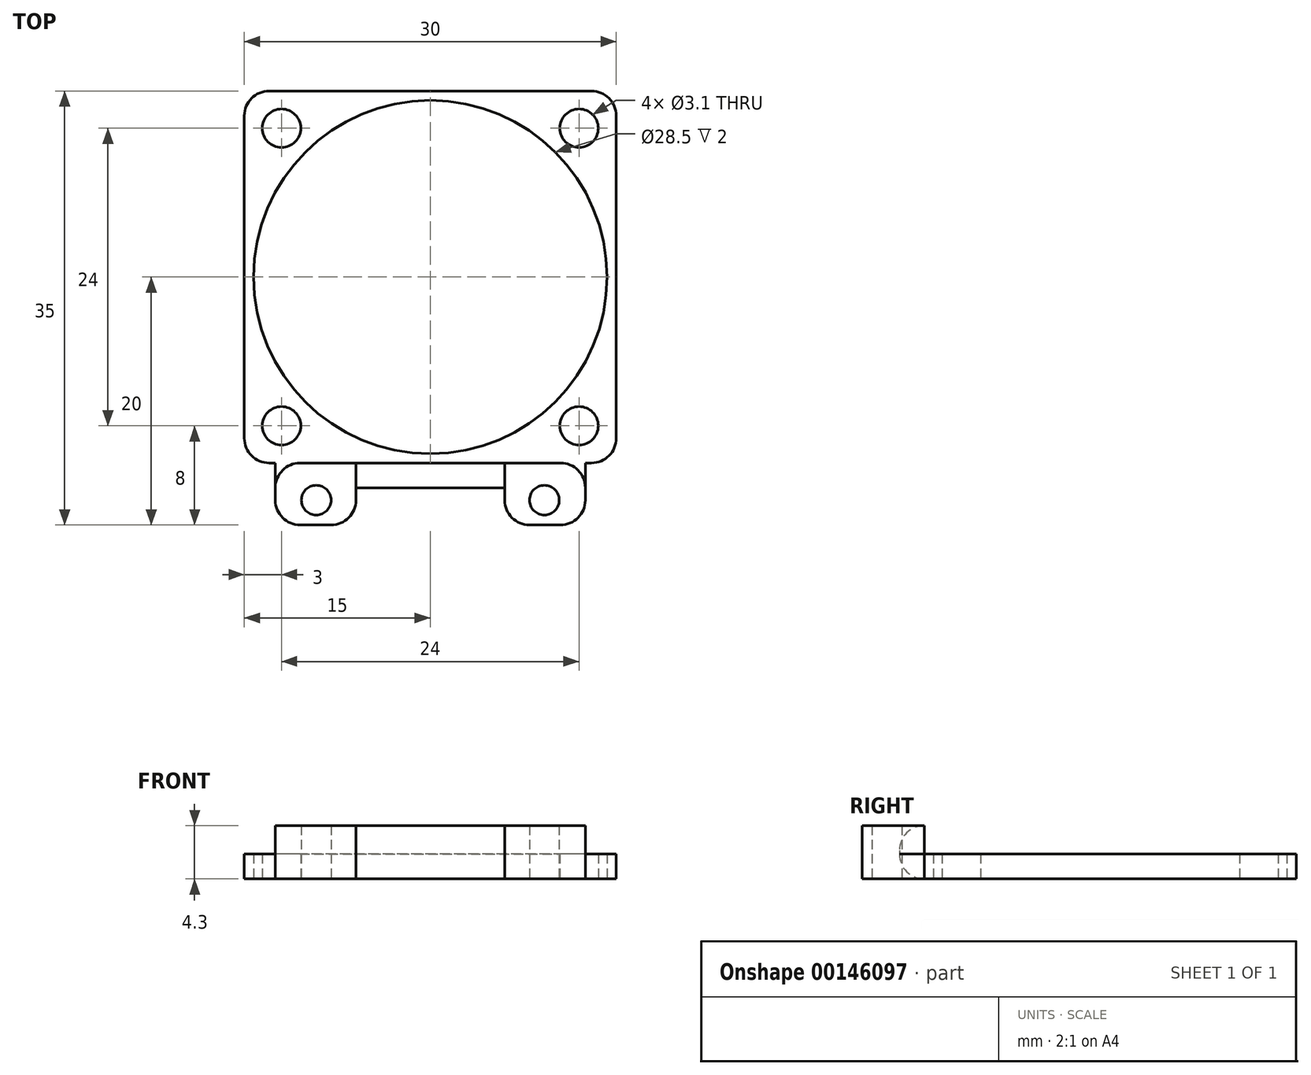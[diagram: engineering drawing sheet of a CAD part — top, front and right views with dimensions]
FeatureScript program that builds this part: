
annotation { "Feature Type Name" : "Feature", "Feature Type Description" : "" }
export const myFeature = defineFeature(function(context is Context, id is Id, definition is map)
    precondition{}
    {
        {
            var Q0;
            Q0=qCreatedBy(makeId("Top.planeOp"),FACE);
            var sketch = newSketch(context, id + "F0", { "sketchPlane" : qUnion([Q0])});
            skLineSegment(sketch, "E0.bottom", {"start": v(15, -15) * mm, "end": v(-15, -15) * mm});
            skLineSegment(sketch, "E0.top", {"start": v(15, 15) * mm, "end": v(-15, 15) * mm});
            skLineSegment(sketch, "E0.left", {"start": v(15, -15) * mm, "end": v(15, 15) * mm});
            skLineSegment(sketch, "E0.right", {"start": v(-15, -15) * mm, "end": v(-15, 15) * mm});
            skPoint(sketch, "E0.middle", {"position": v(0, 0) * mm});
            skLineSegment(sketch, "E1.bottom", {"start": v(12, -12) * mm, "end": v(-12, -12) * mm, "construction": true});
            skLineSegment(sketch, "E1.top", {"start": v(12, 12) * mm, "end": v(-12, 12) * mm, "construction": true});
            skLineSegment(sketch, "E1.left", {"start": v(12, -12) * mm, "end": v(12, 12) * mm, "construction": true});
            skLineSegment(sketch, "E1.right", {"start": v(-12, -12) * mm, "end": v(-12, 12) * mm, "construction": true});
            skCircle(sketch, "E2", {"center": v(-12, 12) * mm, "radius": 1.55 * mm});
            skCircle(sketch, "E3", {"center": v(12, 12) * mm, "radius": 1.55 * mm});
            skCircle(sketch, "E4", {"center": v(12, -12) * mm, "radius": 1.55 * mm});
            skCircle(sketch, "E5", {"center": v(-12, -12) * mm, "radius": 1.55 * mm});
            skLineSegment(sketch, "E6", {"start": v(-14.96, -20) * mm, "end": v(-6, -20) * mm, "construction": true});
            skLineSegment(sketch, "E7.bottom", {"start": v(-15, -15) * mm, "end": v(15, -15) * mm});
            skLineSegment(sketch, "E7.top", {"start": v(-6, -17) * mm, "end": v(6, -17) * mm});
            skLineSegment(sketch, "E8.bottom", {"start": v(-12.5, -15) * mm, "end": v(12.5, -15) * mm});
            skLineSegment(sketch, "E8.top", {"start": v(-12.5, -20) * mm, "end": v(-6, -20) * mm});
            skLineSegment(sketch, "E8.left", {"start": v(-12.5, -15) * mm, "end": v(-12.5, -20) * mm});
            skLineSegment(sketch, "E8.right", {"start": v(12.5, -15) * mm, "end": v(12.5, -20) * mm});
            skLineSegment(sketch, "E9.bottom", {"start": v(-6, -15) * mm, "end": v(6, -15) * mm});
            skLineSegment(sketch, "E9.left", {"start": v(-6, -15) * mm, "end": v(-6, -20) * mm});
            skLineSegment(sketch, "E9.right", {"start": v(6, -15) * mm, "end": v(6, -20) * mm});
            skPoint(sketch, "E7.right.end.orphan", {"position": v(15, -17) * mm});
            skLineSegment(sketch, "E10.trimOffspring", {"start": v(6, -20) * mm, "end": v(15.77, -20) * mm, "construction": true});
            skLineSegment(sketch, "E11.trimOffspring", {"start": v(6, -20) * mm, "end": v(12.5, -20) * mm});
            skLineSegment(sketch, "E12", {"start": v(-13.8, -18) * mm, "end": v(14.7, -18) * mm, "construction": true});
            skLineSegment(sketch, "E13", {"start": v(-9.2, -15) * mm, "end": v(-9.2, -21.94) * mm, "construction": true});
            skLineSegment(sketch, "E14", {"start": v(9.2, -15) * mm, "end": v(9.2, -21.94) * mm, "construction": true});
            skCircle(sketch, "E15", {"center": v(-9.2, -18) * mm, "radius": 1.2 * mm});
            skCircle(sketch, "E16", {"center": v(9.2, -18) * mm, "radius": 1.2 * mm});
            skCircle(sketch, "E17", {"center": v(0, 0) * mm, "radius": 14.25 * mm});
            skSolve(sketch);
        }
        {
            var Q0;
            Q0=makeQuery(id+"F0.imprint","IMPRINT",FACE,{"disambiguationData":[TD([[makeQuery(id+"F0.imprint","IMPRINT",EDGE,{"derivedFrom":sQuery(id+"F0.wireOp",EDGE,"E0.top")}),1.0]])]});
            var Q1;
            {var subQ4=sQuery(id+"F0.wireOp",EDGE,"E8.top");Q1=makeQuery(id+"F0.imprint","IMPRINT",FACE,{"disambiguationData":[TD([[makeQuery(id+"F0.imprint","IMPRINT",EDGE,{"derivedFrom":subQ4}),1.0]])]});}
            var Q2;
            {var subQ0=sQuery(id+"F0.wireOp",EDGE,"E7.top");Q2=makeQuery(id+"F0.imprint","IMPRINT",FACE,{"disambiguationData":[TD([[makeQuery(id+"F0.imprint","IMPRINT",EDGE,{"derivedFrom":subQ0}),1.0]])]});}
            var Q3;
            {var subQ5=sQuery(id+"F0.wireOp",EDGE,"E8.right");Q3=makeQuery(id+"F0.imprint","IMPRINT",FACE,{"disambiguationData":[TD([[makeQuery(id+"F0.imprint","IMPRINT",EDGE,{"derivedFrom":subQ5}),-1.0]])]});}
            extrude(context, id + "F1", {"entities" : qUnion([Q0, Q1, Q2, Q3]), "flatOperationType" : FlatOperationType.REMOVE, "offsetDistance" : 25 * mm, "depth" : 2 * mm, "domain" : OperationDomain.MODEL});
        }
        {
            var Q0;
            {var subQ0=sQuery(id+"F0.wireOp",EDGE,"E7.top");Q0=makeQuery(id+"F0.imprint","IMPRINT",FACE,{"disambiguationData":[TD([[makeQuery(id+"F0.imprint","IMPRINT",EDGE,{"derivedFrom":subQ0}),1.0]])]});}
            var Q1;
            {var subQ4=sQuery(id+"F0.wireOp",EDGE,"E8.top");Q1=makeQuery(id+"F0.imprint","IMPRINT",FACE,{"disambiguationData":[TD([[makeQuery(id+"F0.imprint","IMPRINT",EDGE,{"derivedFrom":subQ4}),1.0]])]});}
            var Q2;
            {var subQ5=sQuery(id+"F0.wireOp",EDGE,"E8.right");Q2=makeQuery(id+"F0.imprint","IMPRINT",FACE,{"disambiguationData":[TD([[makeQuery(id+"F0.imprint","IMPRINT",EDGE,{"derivedFrom":subQ5}),-1.0]])]});}
            extrude(context, id + "F2", {"entities" : qUnion([Q0, Q1, Q2]), "operationType" : NewBodyOperationType.ADD, "flatOperationType" : FlatOperationType.REMOVE, "offsetDistance" : 25 * mm, "depth" : 4.3 * mm, "domain" : OperationDomain.MODEL});
        }
        {
            var Q0;
            Q0=makeQuery(id+"F1.opExtrude","SWEPT_EDGE",EDGE,{"disambiguationData":[OSD([sQuery(id+"F0.wireOp",EDGE,"E0.left"),sQuery(id+"F0.wireOp",EDGE,"E7.bottom")])]});
            var Q1;
            Q1=makeQuery(id+"F1.opExtrude","SWEPT_EDGE",EDGE,{"disambiguationData":[OSD([sQuery(id+"F0.wireOp",EDGE,"E0.right"),sQuery(id+"F0.wireOp",EDGE,"E7.bottom")])]});
            var Q2;
            Q2=makeQuery(id+"F1.opExtrude","SWEPT_EDGE",EDGE,{"disambiguationData":[OSD([sQuery(id+"F0.wireOp",EDGE,"E0.top"),sQuery(id+"F0.wireOp",EDGE,"E0.right")])]});
            var Q3;
            Q3=makeQuery(id+"F1.opExtrude","SWEPT_EDGE",EDGE,{"disambiguationData":[OSD([sQuery(id+"F0.wireOp",EDGE,"E0.top"),sQuery(id+"F0.wireOp",EDGE,"E0.left")])]});
            var Q4;
            {var subQ0=sQuery(id+"F0.wireOp",EDGE,"E8.left");var subQ1=sQuery(id+"F0.wireOp",EDGE,"E8.top");Q4=makeQuery(id+"F2.boolean.opBoolean","MERGE",EDGE,{"derivedFrom":[makeQuery(id+"F1.opExtrude","SWEPT_EDGE",EDGE,{"disambiguationData":[OSD([subQ1,subQ0])]}),makeQuery(id+"F2.opExtrude","SWEPT_EDGE",EDGE,{"disambiguationData":[OSD([subQ1,subQ0])]})]});}
            var Q5;
            {var subQ0=sQuery(id+"F0.wireOp",EDGE,"E9.left");var subQ1=sQuery(id+"F0.wireOp",EDGE,"E8.top");Q5=makeQuery(id+"F2.boolean.opBoolean","MERGE",EDGE,{"derivedFrom":[makeQuery(id+"F1.opExtrude","SWEPT_EDGE",EDGE,{"disambiguationData":[OSD([subQ1,subQ0])]}),makeQuery(id+"F2.opExtrude","SWEPT_EDGE",EDGE,{"disambiguationData":[OSD([subQ1,subQ0])]})]});}
            var Q6;
            {var subQ0=sQuery(id+"F0.wireOp",EDGE,"E11.trimOffspring");var subQ1=sQuery(id+"F0.wireOp",EDGE,"E9.right");Q6=makeQuery(id+"F2.boolean.opBoolean","MERGE",EDGE,{"derivedFrom":[makeQuery(id+"F1.opExtrude","SWEPT_EDGE",EDGE,{"disambiguationData":[OSD([subQ1,subQ0])]}),makeQuery(id+"F2.opExtrude","SWEPT_EDGE",EDGE,{"disambiguationData":[OSD([subQ1,subQ0])]})]});}
            var Q7;
            {var subQ0=sQuery(id+"F0.wireOp",EDGE,"E11.trimOffspring");var subQ1=sQuery(id+"F0.wireOp",EDGE,"E8.right");Q7=makeQuery(id+"F2.boolean.opBoolean","MERGE",EDGE,{"derivedFrom":[makeQuery(id+"F1.opExtrude","SWEPT_EDGE",EDGE,{"disambiguationData":[OSD([subQ1,subQ0])]}),makeQuery(id+"F2.opExtrude","SWEPT_EDGE",EDGE,{"disambiguationData":[OSD([subQ1,subQ0])]})]});}
            var Q8;
            Q8=makeQuery(id+"F2.opExtrude","SWEPT_EDGE",EDGE,{"disambiguationData":[OSD([sQuery(id+"F0.wireOp",EDGE,"E7.bottom"),sQuery(id+"F0.wireOp",EDGE,"E8.bottom"),sQuery(id+"F0.wireOp",EDGE,"E8.right")])]});
            var Q9;
            Q9=makeQuery(id+"F2.opExtrude","SWEPT_EDGE",EDGE,{"disambiguationData":[OSD([sQuery(id+"F0.wireOp",EDGE,"E7.bottom"),sQuery(id+"F0.wireOp",EDGE,"E8.bottom"),sQuery(id+"F0.wireOp",EDGE,"E8.left")])]});
            var Q10;
            Q10=makeQuery(id+"F2.opExtrude","CAP_EDGE",EDGE,{"disambiguationData":[OSD([sQuery(id+"F0.wireOp",EDGE,"E7.top")])],"isStart":false});
            var Q11;
            Q11=makeQuery(id+"F1.opExtrude","CAP_EDGE",EDGE,{"disambiguationData":[OSD([sQuery(id+"F0.wireOp",EDGE,"E7.top")])],"isStart":true});
            fillet(context, id + "F3", {"entities" : qUnion([Q0, Q1, Q2, Q3, Q4, Q5, Q6, Q7, Q8, Q9, Q10, Q11]), "radius" : 2 * mm, "tangentPropagation" : true, "allowEdgeOverflow" : false});
        }
    });
